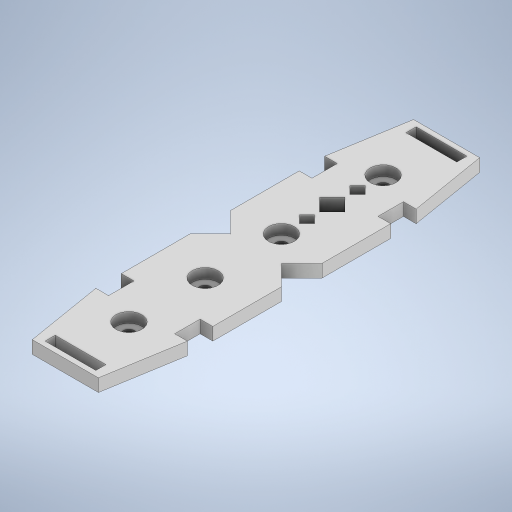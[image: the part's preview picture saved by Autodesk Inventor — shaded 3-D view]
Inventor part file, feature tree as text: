
AUTODESK INVENTOR PART (.ipt)
format: ipt  version: 2023 (Build 270158000, 158)  size: 329,728 bytes
history: native  units: mm
features: extrude x2, sketch x1
ambient origin geometry x8: Origin, YZ Plane, XZ Plane, XY Plane, X Axis, Y Axis, Z Axis, Center Point
bodies: Solid1 (feature_tree)
feature tree (3):
  sketch  "Sketch1"  dims[d2=10.2mm d3=25.0mm d4=10.2mm d5=30.0mm d6=10.2mm d7=30.0mm d8=10.2mm d9=40.0mm d10=25.0mm d12=5.0mm d13=10.0mm d15=10.0mm d17=5.0mm d19=5.0mm d20=5.0mm d21=0.0mm d22=4.5mm d23=4.5mm d24=4.5mm d25=4.5mm d26=1.0mm d27=0.0mm d38=3.0mm d39=2.0mm d41=2.0mm d42=4.0mm d44=2.0mm d45=3.0mm d46=4.0mm d50=8.0mm d51=8.0mm]
  extrude  "Extrusion1"  Depth=8.0mm
  extrude  "Extrusion2"  Depth=8.0mm
